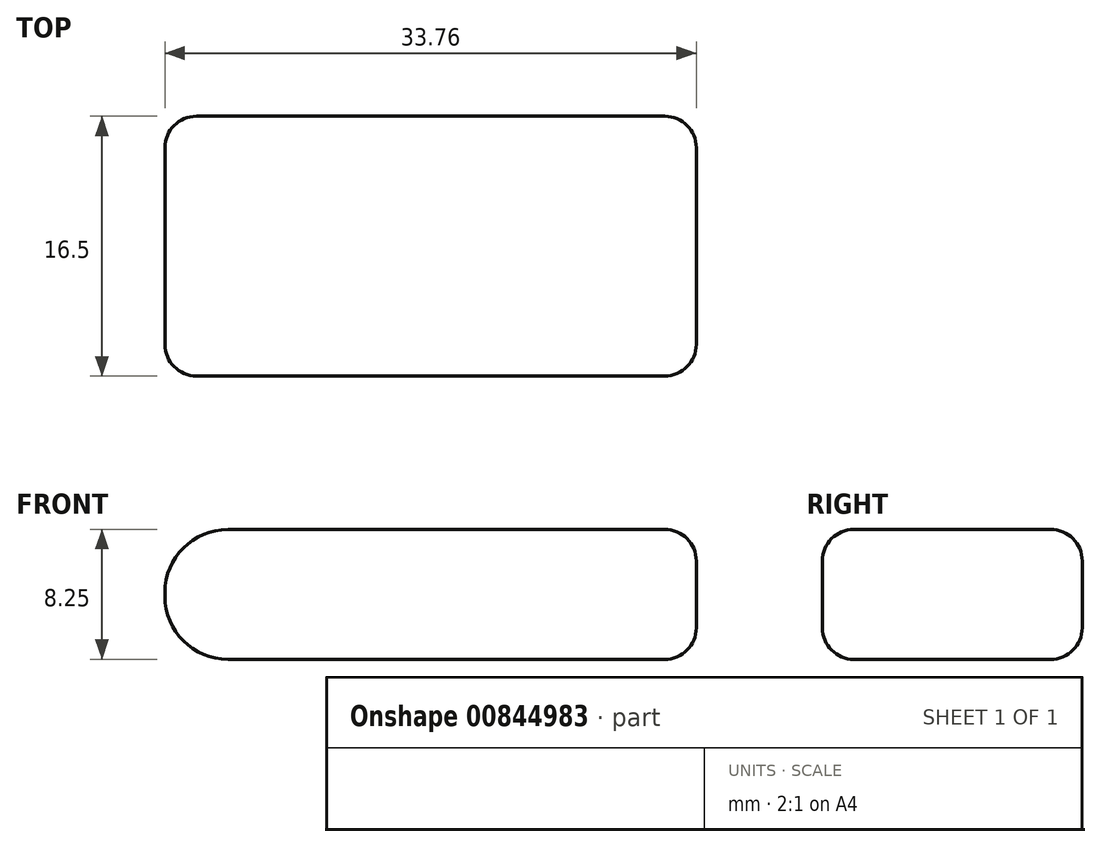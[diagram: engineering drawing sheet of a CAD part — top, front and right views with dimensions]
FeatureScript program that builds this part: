
annotation { "Feature Type Name" : "Feature", "Feature Type Description" : "" }
export const myFeature = defineFeature(function(context is Context, id is Id, definition is map)
    precondition{}
    {
        {
            var Q0;
            Q0=qCreatedBy(makeId("Top.planeOp"),FACE);
            var sketch = newSketch(context, id + "F0", { "sketchPlane" : qUnion([Q0])});
            skLineSegment(sketch, "E0.bottom", {"start": v(-16.87, 8.25) * mm, "end": v(16.88, 8.25) * mm});
            skLineSegment(sketch, "E0.top", {"start": v(-16.88, -8.25) * mm, "end": v(16.88, -8.25) * mm});
            skLineSegment(sketch, "E0.left", {"start": v(-16.87, 8.25) * mm, "end": v(-16.88, -8.25) * mm});
            skLineSegment(sketch, "E0.right", {"start": v(16.88, 8.25) * mm, "end": v(16.88, -8.25) * mm});
            skPoint(sketch, "E0.middle", {"position": v(0, 0) * mm});
            skSolve(sketch);
        }
        {
            var Q0;
            Q0=makeQuery(id+"F0.imprint","IMPRINT",FACE,{"disambiguationData":[TD([[makeQuery(id+"F0.imprint","IMPRINT",EDGE,{"derivedFrom":sQuery(id+"F0.wireOp",EDGE,"E0.bottom")}),-1.0]])]});
            extrude(context, id + "F1", {"entities" : qUnion([Q0]), "depth" : 8.25 * mm, "offsetDistance" : 25 * mm});
        }
        {
            var Q0;
            Q0=makeQuery(id+"F1.opExtrude","CAP_EDGE",EDGE,{"disambiguationData":[OSD([sQuery(id+"F0.wireOp",EDGE,"E0.left")])],"isStart":false});
            var Q1;
            Q1=makeQuery(id+"F1.opExtrude","CAP_EDGE",EDGE,{"disambiguationData":[OSD([sQuery(id+"F0.wireOp",EDGE,"E0.left")])],"isStart":true});
            fillet(context, id + "F2", {"entities" : qUnion([Q0, Q1]), "radius" : 4 * mm, "tangentPropagation" : true, "allowEdgeOverflow" : false});
        }
        {
            var Q0;
            Q0=makeQuery(id+"F1.opExtrude","CAP_EDGE",EDGE,{"disambiguationData":[OSD([sQuery(id+"F0.wireOp",EDGE,"E0.top")])],"isStart":false});
            var Q1;
            Q1=makeQuery(id+"F1.opExtrude","CAP_EDGE",EDGE,{"disambiguationData":[OSD([sQuery(id+"F0.wireOp",EDGE,"E0.bottom")])],"isStart":false});
            var Q2;
            Q2=makeQuery(id+"F1.opExtrude","CAP_EDGE",EDGE,{"disambiguationData":[OSD([sQuery(id+"F0.wireOp",EDGE,"E0.right")])],"isStart":false});
            var Q3;
            Q3=makeQuery(id+"F1.opExtrude","CAP_EDGE",EDGE,{"disambiguationData":[OSD([sQuery(id+"F0.wireOp",EDGE,"E0.right")])],"isStart":true});
            var Q4;
            Q4=makeQuery(id+"F1.opExtrude","SWEPT_FACE",FACE,{"disambiguationData":[OSD([sQuery(id+"F0.wireOp",EDGE,"E0.right")])]});
            fillet(context, id + "F3", {"entities" : qUnion([Q0, Q1, Q2, Q3, Q4]), "radius" : 2 * mm, "tangentPropagation" : true, "allowEdgeOverflow" : false});
        }
    });
